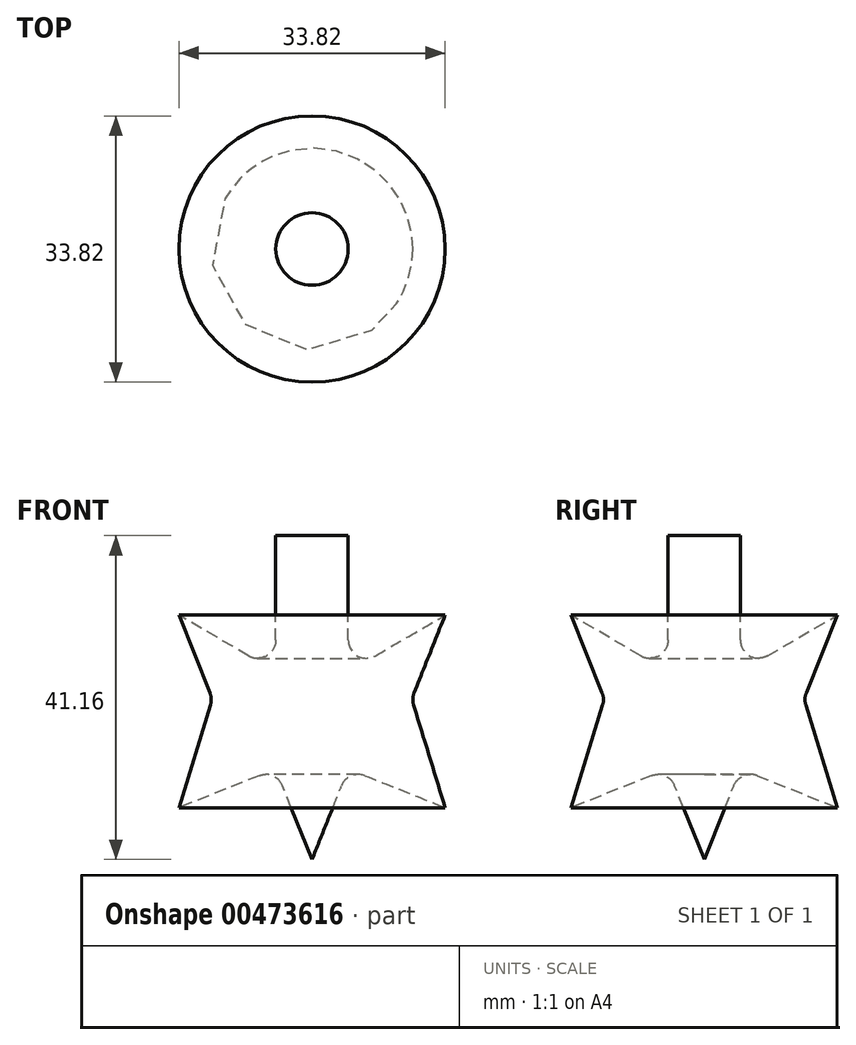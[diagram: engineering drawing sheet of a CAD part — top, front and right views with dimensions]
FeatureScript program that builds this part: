
annotation { "Feature Type Name" : "Feature", "Feature Type Description" : "" }
export const myFeature = defineFeature(function(context is Context, id is Id, definition is map)
    precondition{}
    {
        {
            var Q0;
            Q0=qCreatedBy(makeId("Front.planeOp"),FACE);
            var sketch = newSketch(context, id + "F0", { "sketchPlane" : qUnion([Q0])});
            skLineSegment(sketch, "E0", {"start": v(0, 0) * mm, "end": v(3.75, 9.38) * mm});
            skLineSegment(sketch, "E1", {"start": v(6.74, 10.66) * mm, "end": v(16.91, 6.59) * mm});
            skLineSegment(sketch, "E2", {"start": v(16.91, 6.59) * mm, "end": v(12.9, 19.66) * mm});
            skLineSegment(sketch, "E3", {"start": v(12.96, 21.19) * mm, "end": v(16.91, 31.05) * mm});
            skLineSegment(sketch, "E4", {"start": v(16.91, 31.05) * mm, "end": v(8.05, 25.9) * mm});
            skLineSegment(sketch, "E5", {"start": v(4.6, 27.88) * mm, "end": v(4.6, 41.16) * mm});
            skLineSegment(sketch, "E6", {"start": v(4.6, 41.16) * mm, "end": v(0, 41.16) * mm});
            skLineSegment(sketch, "E7", {"start": v(0, 41.16) * mm, "end": v(0, 0) * mm});
            skPoint(sketch, "E8.visualSharp", {"position": v(4.6, 23.89) * mm});
            skArc(sketch, "E8.filletArc", {"start": v(4.6, 27.88) * mm, "mid": v(5.76, 25.89) * mm, "end": v(8.05, 25.9) * mm});
            skPoint(sketch, "E9.visualSharp", {"position": v(12.66, 20.43) * mm});
            skArc(sketch, "E9.filletArc", {"start": v(12.96, 21.19) * mm, "mid": v(12.8, 20.43) * mm, "end": v(12.9, 19.66) * mm});
            skPoint(sketch, "E10.visualSharp", {"position": v(4.6, 11.51) * mm});
            skArc(sketch, "E10.filletArc", {"start": v(6.74, 10.66) * mm, "mid": v(4.98, 10.64) * mm, "end": v(3.75, 9.38) * mm});
            skSolve(sketch);
        }
        {
            var Q0;
            Q0=makeQuery(id+"F0.imprint","IMPRINT",FACE,{"disambiguationData":[TD([[makeQuery(id+"F0.imprint","IMPRINT",EDGE,{"derivedFrom":sQuery(id+"F0.wireOp",EDGE,"E0")}),1.0]])]});
            var Q1;
            Q1=sQuery(id+"F0.wireOp",EDGE,"E7");
            revolve(context, id + "F1", {"entities" : qUnion([Q0]), "axis" : qUnion([Q1]), "revolveType" : RevolveType.FULL});
        }
    });
